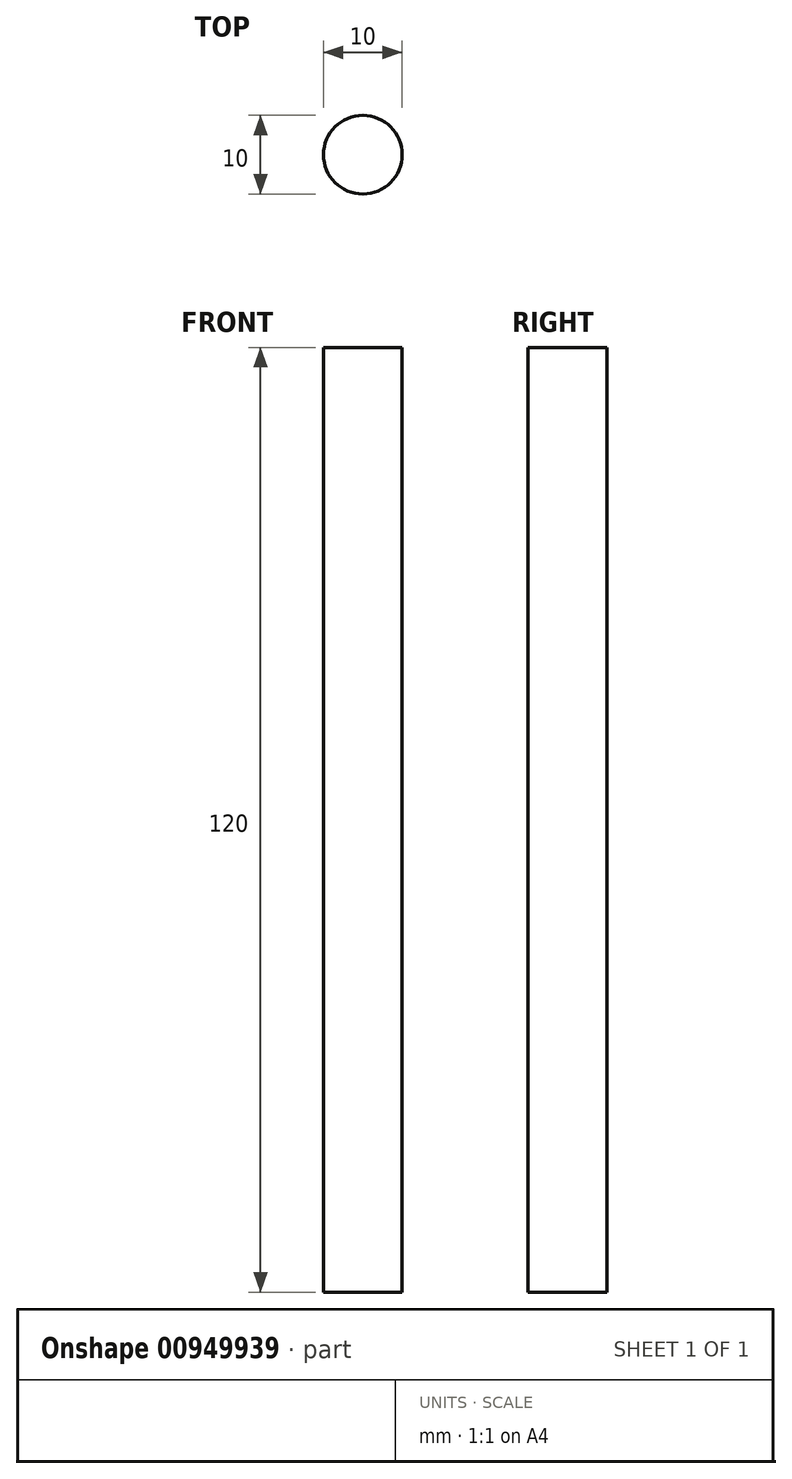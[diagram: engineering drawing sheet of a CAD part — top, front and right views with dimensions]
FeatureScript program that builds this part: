
annotation { "Feature Type Name" : "Feature", "Feature Type Description" : "" }
export const myFeature = defineFeature(function(context is Context, id is Id, definition is map)
    precondition{}
    {
        {
            var Q0;
            Q0=qCreatedBy(makeId("Top.planeOp"),FACE);
            var sketch = newSketch(context, id + "F0", { "sketchPlane" : qUnion([Q0])});
            skCircle(sketch, "E0", {"center": v(0, 0) * mm, "radius": 5 * mm});
            skSolve(sketch);
        }
        {
            var Q0;
            Q0=makeQuery(id+"F0.imprint","IMPRINT",FACE,{"disambiguationData":[TD([[makeQuery(id+"F0.imprint","IMPRINT",EDGE,{"derivedFrom":sQuery(id+"F0.wireOp",EDGE,"E0")}),1.0]])]});
            extrude(context, id + "F1", {"entities" : qUnion([Q0]), "depth" : 120 * mm, "offsetDistance" : 25 * mm});
        }
    });
